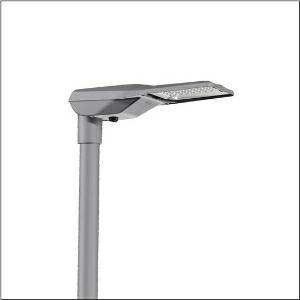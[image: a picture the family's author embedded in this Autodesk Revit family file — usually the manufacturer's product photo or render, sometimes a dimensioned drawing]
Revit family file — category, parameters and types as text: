
# Revit family: streetlight_sl_21_iq_mini___p0_8a_5xe2u31u08hb_1639
name_source: partatom
category: Lighting Fixtures
units: mm (PartAtom-declared; Revit-internal decimal feet)

## family parameters
Cut with Voids When Loaded = No
Host = Face
Light Source = No
Part Type = Normal
Room Calculation Point = No
Round Connector Dimension = Use Diameter
Shared = No

## types (1)
- --- (1 x LED, 9830 lm, 71 W, 3000K)
    Apparent Load = 71 VA
    CIE Flux Codes = 33 69 96 100 100
    Color Rendering = 70
    Color Temperature = 3000K
    Default Elevation = 1800 mm
    Description = Streetlight SL 21 iQ mini, mast luminaire, primary light control with lens, of PMMA, primary optical cover: cover, of toughened safety glass, transparent, light distribution: P0.8a, light emission: direct distribution, primary light characteristic: asymmetric, installation type: post-top, side-entry, LED, High Power LED, rated luminous flux: 9.830lm, luminous efficacy: 139lm/W, light colour: 730, colour temperature: 3000K, control gear: iQ-Street Remote, D4i with power reduction, control: pre-setting: logarithmic dimming characteristic, Street-Remote, Auto-Match, Temp-Guard, Lumen-Switch, Night-Set, Smart-Wire, Light-Fading, Desk-Remote (wireless, voltage-free reading and setting of iQ features in the workshop via application-optimized NFC function/RFID function), optimised constant luminous flux control (CLO 2.0), mains connection: 220..240V, AC, 50/60Hz, start of lifetime: 71W, end of service life: 75W, reduction: 30W, luminaire housing, of diecast aluminium, powder-coated, SITECO metallic grey (DB 702S), corrosivity category C5 high according to DIN EN ISO 12944, please order mast flange separately, inclination adjustable: 0°, 5°, 10°, 15°, sealing non-destructively replaceable, multi-level sealing system, length: 628mm, width: 235mm, height: 110mm, mast flange for spigot size: 42mm (side-entry): 5XC10008XM4, 60/48mm (side-entry/post-top): 5XC10108XM2, 76/60mm (side-entry/post-top): 5XC10108XM1, mounting height: 4..8m, Smart Interface below, protection rating (complete): IP66, insulation class (complete): insulation class II (safety insulation), certification: CE, ENEC, ENEC+, VDE, impact resistance: IK10, permissible operating ambient temperature for outdoor applications: -40..+50°C, standard-compliant lighting for roads and squares, packaging unit: 1 piece

Light Distribution: P0.8a
    Height = 110 mm
    Lamp = 1 x LED
    Lamp Light Flux = 9830 lm
    Lamp Power = 71 W
    Lamp count = 1
    Length = 625 mm
    Luminous efficacy = 138 lm/W
    Manufacturer = Siteco
    ModVariant = No
    Model = 5XE2U31U08HB
    Number of Poles = 1
    OnlyDefault = Yes
    Power Factor = 1
    Product Name = Streetlight SL 21 iQ mini | P0.8a
    Product group = mast luminaire | pylon top
    ProductGroupID = 6100
    Protection Class = Protection class II
    Protection Degree = IP 66
    RLX_Detail_Level = 1
    RLX_Emergency_Light_Flux = 0 lm
    RLX_Emergency_Type = 0
    RLX_Emergency_Type_DB = No
    RlxData = <blob elided: 92397 chars, md5=e0043d83>
    Socket = socket
    Standby Power = 0 W
    System Light Flux = 9830 lm
    System Power = 71 W
    Type Comments = factory setting: luminous flux: 100 % | dim-lin: 254 | 716 mA
    Type Image = l_1003516.jpg
    URL = http://relux.com
    VarID = @adj_081919
    Voltage = 0 V
    Weight = 0.00 kg
    Width = 234 mm

## geometry (parser evidence)
native form markers: Blend x4, Sweep x10
no freeform markers — native parametric forms only
